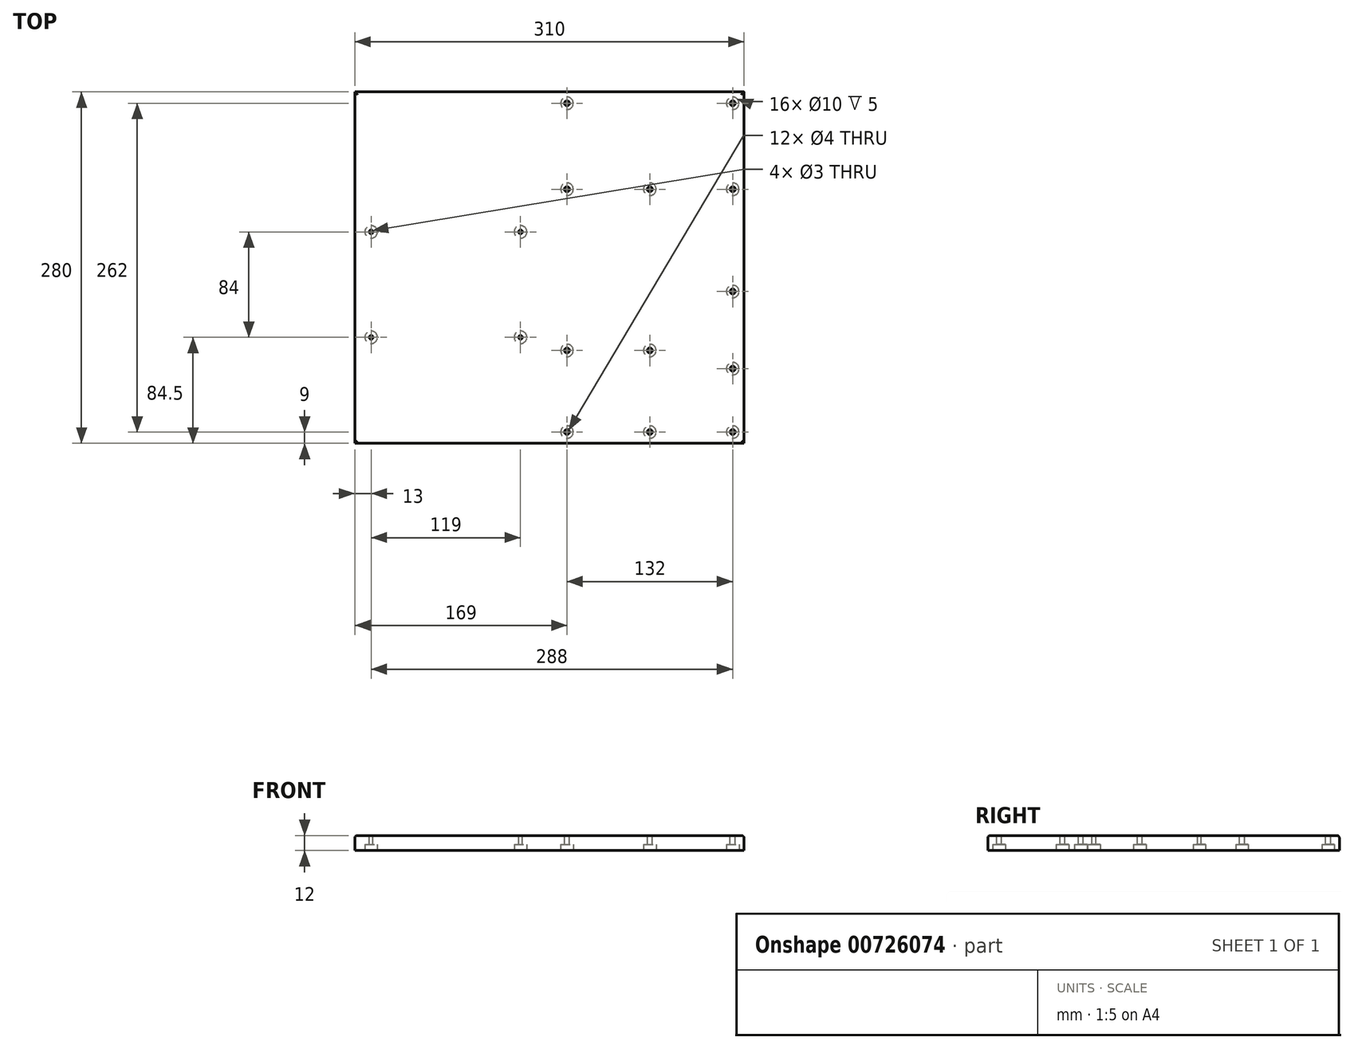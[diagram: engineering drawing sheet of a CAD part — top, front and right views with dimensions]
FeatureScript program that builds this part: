
annotation { "Feature Type Name" : "Feature", "Feature Type Description" : "" }
export const myFeature = defineFeature(function(context is Context, id is Id, definition is map)
    precondition{}
    {
        {
            var Q0;
            Q0=qCreatedBy(makeId("Top.planeOp"),FACE);
            var sketch = newSketch(context, id + "F0", { "sketchPlane" : qUnion([Q0])});
            skLineSegment(sketch, "E0.bottom", {"start": v(155, -140) * mm, "end": v(-155, -140) * mm});
            skLineSegment(sketch, "E0.top", {"start": v(155, 140) * mm, "end": v(-155, 140) * mm});
            skLineSegment(sketch, "E0.left", {"start": v(155, -140) * mm, "end": v(155, 140) * mm});
            skLineSegment(sketch, "E0.right", {"start": v(-155, -140) * mm, "end": v(-155, 140) * mm});
            skPoint(sketch, "E0.middle", {"position": v(0, 0) * mm});
            skSolve(sketch);
        }
        {
            var Q0;
            Q0=makeQuery(id+"F0.imprint","IMPRINT",FACE,{"disambiguationData":[TD([[makeQuery(id+"F0.imprint","IMPRINT",EDGE,{"derivedFrom":sQuery(id+"F0.wireOp",EDGE,"E0.bottom")}),-1.0]])]});
            extrude(context, id + "F1", {"entities" : qUnion([Q0]), "depth" : 12 * mm, "offsetDistance" : 25 * mm});
        }
        {
            var Q0;
            Q0=makeQuery(id+"F1.opExtrude","CAP_FACE",FACE,{"disambiguationData":[OSD([sQuery(id+"F0.wireOp",EDGE,"E0.bottom"),sQuery(id+"F0.wireOp",EDGE,"E0.top"),sQuery(id+"F0.wireOp",EDGE,"E0.left"),sQuery(id+"F0.wireOp",EDGE,"E0.right")])],"isStart":false});
            fillet(context, id + "F2", {"entities" : qUnion([Q0]), "radius" : 2 * mm, "tangentPropagation" : true, "allowEdgeOverflow" : false});
        }
        {
            var Q0;
            Q0=makeQuery(id+"F1.opExtrude","CAP_FACE",FACE,{"disambiguationData":[OSD([sQuery(id+"F0.wireOp",EDGE,"E0.bottom"),sQuery(id+"F0.wireOp",EDGE,"E0.top"),sQuery(id+"F0.wireOp",EDGE,"E0.left"),sQuery(id+"F0.wireOp",EDGE,"E0.right")])],"isStart":false});
            var sketch = newSketch(context, id + "F3", { "sketchPlane" : qUnion([Q0])});
            skLineSegment(sketch, "E1", {"start": v(-196.78, 0) * mm, "end": v(191.88, 0) * mm, "construction": true});
            skLineSegment(sketch, "E2", {"start": v(0, 157.57) * mm, "end": v(0, -128.27) * mm, "construction": true});
            skLineSegment(sketch, "E3", {"start": v(-200.75, 131) * mm, "end": v(221.24, 131) * mm, "construction": true});
            skLineSegment(sketch, "E4", {"start": v(-219.48, -131) * mm, "end": v(210.32, -131) * mm, "construction": true});
            skLineSegment(sketch, "E5", {"start": v(146, 162.68) * mm, "end": v(146, -159.38) * mm, "construction": true});
            skLineSegment(sketch, "E6", {"start": v(14, 134.7) * mm, "end": v(14, -161.99) * mm, "construction": true});
            skCircle(sketch, "E7", {"center": v(14, -131) * mm, "radius": 2 * mm});
            skCircle(sketch, "E8", {"center": v(14, 131) * mm, "radius": 2 * mm});
            skCircle(sketch, "E9", {"center": v(146, 131) * mm, "radius": 2 * mm});
            skCircle(sketch, "E10", {"center": v(146, -131) * mm, "radius": 2 * mm});
            skCircle(sketch, "E11", {"center": v(146, 62.5) * mm, "radius": 2 * mm});
            skCircle(sketch, "E12", {"center": v(146, -80.5) * mm, "radius": 2 * mm});
            skCircle(sketch, "E13", {"center": v(14, -66) * mm, "radius": 2 * mm});
            skCircle(sketch, "E14", {"center": v(14, 62.5) * mm, "radius": 2 * mm});
            skLineSegment(sketch, "E15", {"start": v(80, 143.04) * mm, "end": v(80, -143.04) * mm, "construction": true});
            skCircle(sketch, "E16", {"center": v(80, 62.5) * mm, "radius": 2 * mm});
            skCircle(sketch, "E17", {"center": v(80, -66) * mm, "radius": 2 * mm});
            skCircle(sketch, "E18", {"center": v(146, -19) * mm, "radius": 2 * mm});
            skCircle(sketch, "E19", {"center": v(80, -131) * mm, "radius": 2 * mm});
            skSolve(sketch);
        }
        {
            var Q0;
            Q0=qSketchRegion(id+"F3",true);
            extrude(context, id + "F4", {"entities" : qUnion([Q0]), "operationType" : NewBodyOperationType.REMOVE, "oppositeDirection" : true, "depth" : 25 * mm, "offsetDistance" : 25 * mm});
        }
        {
            var Q0;
            Q0=makeQuery(id+"F1.opExtrude","CAP_FACE",FACE,{"disambiguationData":[OSD([sQuery(id+"F0.wireOp",EDGE,"E0.bottom"),sQuery(id+"F0.wireOp",EDGE,"E0.top"),sQuery(id+"F0.wireOp",EDGE,"E0.left"),sQuery(id+"F0.wireOp",EDGE,"E0.right")])],"isStart":true});
            var sketch = newSketch(context, id + "F5", { "sketchPlane" : qUnion([Q0])});
            skCircle(sketch, "E20", {"center": v(14, 131) * mm, "radius": 5 * mm});
            skCircle(sketch, "E21", {"center": v(14, 66) * mm, "radius": 5 * mm});
            skCircle(sketch, "E22", {"center": v(146, 80.5) * mm, "radius": 5 * mm});
            skCircle(sketch, "E23", {"center": v(146, 131) * mm, "radius": 5 * mm});
            skCircle(sketch, "E24", {"center": v(146, -62.5) * mm, "radius": 5 * mm});
            skCircle(sketch, "E25", {"center": v(14, -62.5) * mm, "radius": 5 * mm});
            skCircle(sketch, "E26", {"center": v(14, -131) * mm, "radius": 5 * mm});
            skCircle(sketch, "E27", {"center": v(146, -131) * mm, "radius": 5 * mm});
            skCircle(sketch, "E28", {"center": v(80, -62.5) * mm, "radius": 5 * mm});
            skCircle(sketch, "E29", {"center": v(80, 66) * mm, "radius": 5 * mm});
            skCircle(sketch, "E30", {"center": v(146, 19) * mm, "radius": 5 * mm});
            skCircle(sketch, "E31", {"center": v(80, 131) * mm, "radius": 5 * mm});
            skSolve(sketch);
        }
        {
            var Q0;
            Q0=qSketchRegion(id+"F5",true);
            extrude(context, id + "F6", {"entities" : qUnion([Q0]), "operationType" : NewBodyOperationType.REMOVE, "oppositeDirection" : true, "depth" : 5 * mm, "offsetDistance" : 25 * mm});
        }
        {
            var Q0;
            Q0=makeQuery(id+"F1.opExtrude","CAP_FACE",FACE,{"disambiguationData":[OSD([sQuery(id+"F0.wireOp",EDGE,"E0.bottom"),sQuery(id+"F0.wireOp",EDGE,"E0.top"),sQuery(id+"F0.wireOp",EDGE,"E0.left"),sQuery(id+"F0.wireOp",EDGE,"E0.right")])],"isStart":false});
            var sketch = newSketch(context, id + "F7", { "sketchPlane" : qUnion([Q0])});
            skLineSegment(sketch, "E32", {"start": v(130.13, -55.5) * mm, "end": v(-146.46, -55.5) * mm, "construction": true});
            skPoint(sketch, "E33", {"position": v(14, -66) * mm});
            skLineSegment(sketch, "E34", {"start": v(111.7, 28.5) * mm, "end": v(-150.71, 28.5) * mm, "construction": true});
            skLineSegment(sketch, "E35", {"start": v(-23, 50.44) * mm, "end": v(-23, -80.35) * mm, "construction": true});
            skLineSegment(sketch, "E36", {"start": v(-142, 63.64) * mm, "end": v(-142, -75.13) * mm, "construction": true});
            skCircle(sketch, "E37", {"center": v(-142, 28.5) * mm, "radius": 1.5 * mm});
            skCircle(sketch, "E38", {"center": v(-23, 28.5) * mm, "radius": 1.5 * mm});
            skCircle(sketch, "E39", {"center": v(-23, -55.5) * mm, "radius": 1.5 * mm});
            skCircle(sketch, "E40", {"center": v(-142, -55.5) * mm, "radius": 1.5 * mm});
            skSolve(sketch);
        }
        {
            var Q0;
            Q0=qSketchRegion(id+"F7",true);
            extrude(context, id + "F8", {"entities" : qUnion([Q0]), "operationType" : NewBodyOperationType.REMOVE, "oppositeDirection" : true, "depth" : 25 * mm, "offsetDistance" : 25 * mm});
        }
        {
            var Q0;
            Q0=makeQuery(id+"F1.opExtrude","CAP_FACE",FACE,{"disambiguationData":[OSD([sQuery(id+"F0.wireOp",EDGE,"E0.bottom"),sQuery(id+"F0.wireOp",EDGE,"E0.top"),sQuery(id+"F0.wireOp",EDGE,"E0.left"),sQuery(id+"F0.wireOp",EDGE,"E0.right")])],"isStart":true});
            var sketch = newSketch(context, id + "F9", { "sketchPlane" : qUnion([Q0])});
            skCircle(sketch, "E41", {"center": v(-142, 55.5) * mm, "radius": 5 * mm});
            skCircle(sketch, "E42", {"center": v(-142, -28.5) * mm, "radius": 5 * mm});
            skCircle(sketch, "E43", {"center": v(-23, -28.5) * mm, "radius": 5 * mm});
            skCircle(sketch, "E44", {"center": v(-23, 55.5) * mm, "radius": 5 * mm});
            skSolve(sketch);
        }
        {
            var Q0;
            Q0=qSketchRegion(id+"F9",true);
            extrude(context, id + "F10", {"entities" : qUnion([Q0]), "operationType" : NewBodyOperationType.REMOVE, "oppositeDirection" : true, "depth" : 5 * mm, "offsetDistance" : 25 * mm});
        }
    });
